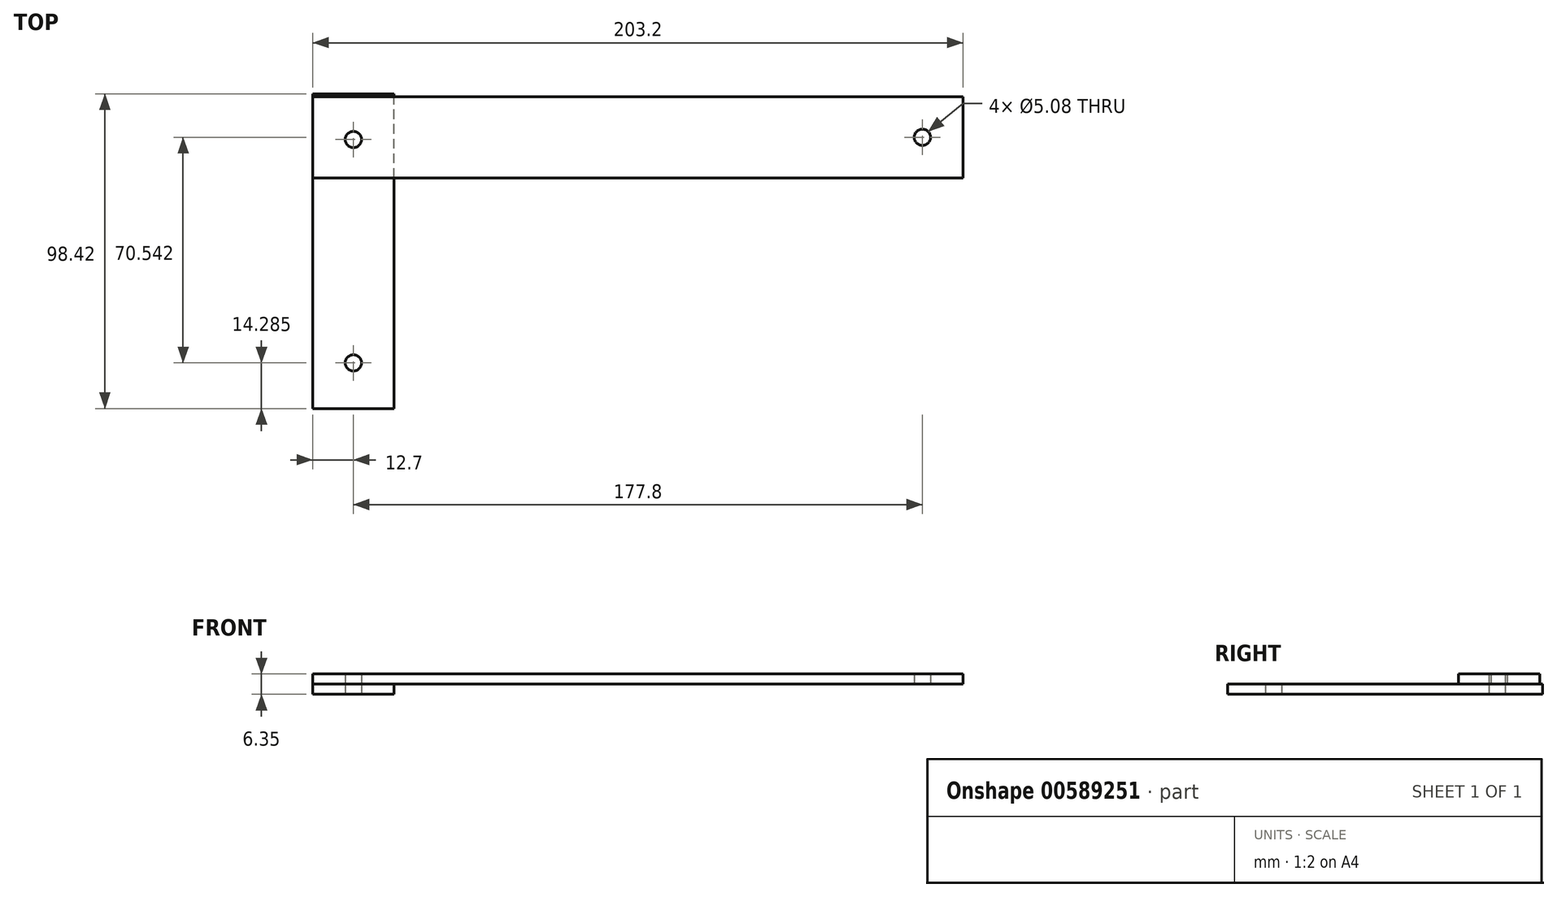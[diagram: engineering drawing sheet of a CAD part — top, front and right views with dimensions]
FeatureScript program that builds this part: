
annotation { "Feature Type Name" : "Feature", "Feature Type Description" : "" }
export const myFeature = defineFeature(function(context is Context, id is Id, definition is map)
    precondition{}
    {
        {
            var Q0;
            Q0=qCreatedBy(makeId("Top.planeOp"),FACE);
            var sketch = newSketch(context, id + "F0", { "sketchPlane" : qUnion([Q0])});
            skLineSegment(sketch, "E0.bottom", {"start": v(12.7, -49.21) * mm, "end": v(-12.7, -49.21) * mm});
            skLineSegment(sketch, "E0.top", {"start": v(12.7, 49.21) * mm, "end": v(-12.7, 49.21) * mm});
            skLineSegment(sketch, "E0.left", {"start": v(12.7, -49.21) * mm, "end": v(12.7, 49.21) * mm});
            skLineSegment(sketch, "E0.right", {"start": v(-12.7, -49.21) * mm, "end": v(-12.7, 49.21) * mm});
            skPoint(sketch, "E0.middle", {"position": v(0, 0) * mm});
            skLineSegment(sketch, "E1", {"start": v(-7.58, 34.92) * mm, "end": v(8.21, 34.92) * mm, "construction": true});
            skLineSegment(sketch, "E2", {"start": v(-6.38, -34.92) * mm, "end": v(7.87, -34.92) * mm, "construction": true});
            skCircle(sketch, "E3", {"center": v(0, 34.92) * mm, "radius": 2.54 * mm});
            skCircle(sketch, "E4", {"center": v(0, -34.92) * mm, "radius": 2.54 * mm});
            skPoint(sketch, "E4.centerSnap0", {"position": v(0.74, -34.92) * mm});
            skSolve(sketch);
        }
        {
            var Q0;
            Q0=makeQuery(id+"F0.imprint","IMPRINT",FACE,{"disambiguationData":[TD([[makeQuery(id+"F0.imprint","IMPRINT",EDGE,{"derivedFrom":sQuery(id+"F0.wireOp",EDGE,"E0.bottom")}),-1.0]])]});
            extrude(context, id + "F1", {"entities" : qUnion([Q0]), "depth" : (1 / 8 * 25.4) * mm, "offsetDistance" : 25 * mm});
        }
        {
            var Q0;
            Q0=makeQuery(id+"F1.opExtrude","CAP_FACE",FACE,{"disambiguationData":[OSD([sQuery(id+"F0.wireOp",EDGE,"E0.bottom"),sQuery(id+"F0.wireOp",EDGE,"E0.top"),sQuery(id+"F0.wireOp",EDGE,"E0.left"),sQuery(id+"F0.wireOp",EDGE,"E0.right"),sQuery(id+"F0.wireOp",EDGE,"E3"),sQuery(id+"F0.wireOp",EDGE,"E4")])],"isStart":false});
            var sketch = newSketch(context, id + "F2", { "sketchPlane" : qUnion([Q0])});
            skCircle(sketch, "E5", {"center": v(0, 34.92) * mm, "radius": 2.54 * mm});
            skLineSegment(sketch, "E6.bottom", {"start": v(-12.7, 48.32) * mm, "end": v(190.5, 48.32) * mm});
            skLineSegment(sketch, "E6.top", {"start": v(-12.7, 22.92) * mm, "end": v(190.5, 22.92) * mm});
            skLineSegment(sketch, "E6.left", {"start": v(-12.7, 48.32) * mm, "end": v(-12.7, 22.92) * mm});
            skLineSegment(sketch, "E6.right", {"start": v(190.5, 48.32) * mm, "end": v(190.5, 22.92) * mm});
            skLineSegment(sketch, "E7", {"start": v(181.3, 35.62) * mm, "end": v(174.55, 35.62) * mm, "construction": true});
            skPoint(sketch, "E7.startSnap0", {"position": v(190.5, 35.62) * mm});
            skLineSegment(sketch, "E8", {"start": v(177.8, 43.71) * mm, "end": v(177.8, 27.52) * mm, "construction": true});
            skCircle(sketch, "E9", {"center": v(177.8, 35.62) * mm, "radius": 2.54 * mm});
            skSolve(sketch);
        }
        {
            var Q0;
            {var subQ0=sQuery(id+"F2.wireOp",EDGE,"E6.right");Q0=makeQuery(id+"F2.imprint","IMPRINT",FACE,{"disambiguationData":[TD([[makeQuery(id+"F2.imprint","IMPRINT",EDGE,{"derivedFrom":subQ0}),-1.0]])]});}
            var Q1;
            Q1=makeQuery(id+"F2.imprint","IMPRINT",FACE,{"disambiguationData":[TD([[makeQuery(id+"F2.imprint","IMPRINT",EDGE,{"derivedFrom":sQuery(id+"F2.wireOp",EDGE,"E5")}),-1.0]])]});
            extrude(context, id + "F3", {"entities" : qUnion([Q0, Q1]), "depth" : (1 / 8 * 25.4) * mm, "offsetDistance" : 25 * mm});
        }
    });
